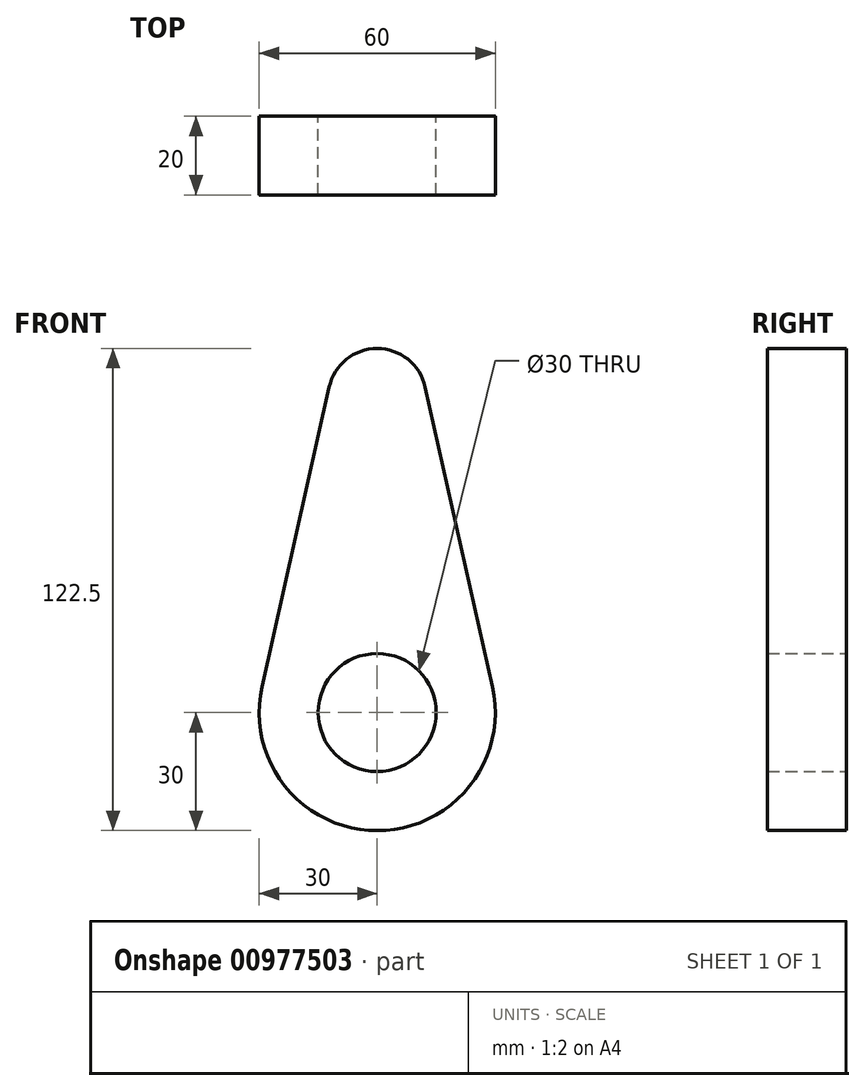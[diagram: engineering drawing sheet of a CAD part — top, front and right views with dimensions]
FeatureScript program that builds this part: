
annotation { "Feature Type Name" : "Feature", "Feature Type Description" : "" }
export const myFeature = defineFeature(function(context is Context, id is Id, definition is map)
    precondition{}
    {
        {
            var Q0;
            Q0=qCreatedBy(makeId("Front.planeOp"),FACE);
            var sketch = newSketch(context, id + "F0", { "sketchPlane" : qUnion([Q0])});
            skArc(sketch, "E0", {"start": v(-29.27, -33.44) * mm, "mid": v(0, -70) * mm, "end": v(29.27, -33.44) * mm});
            skArc(sketch, "E1", {"start": v(12.2, 42.73) * mm, "mid": v(0, 52.5) * mm, "end": v(-12.2, 42.73) * mm});
            skLineSegment(sketch, "E2", {"start": v(-12.2, 42.73) * mm, "end": v(-29.27, -33.44) * mm});
            skLineSegment(sketch, "E3", {"start": v(0, 77.79) * mm, "end": v(0, 52.5) * mm, "construction": true});
            skLineSegment(sketch, "E4.MirrorCS", {"start": v(12.2, 42.73) * mm, "end": v(29.27, -33.44) * mm});
            skPoint(sketch, "E5.orphan", {"position": v(-7, 65.88) * mm});
            skPoint(sketch, "E6.orphan", {"position": v(7, 65.88) * mm});
            skPoint(sketch, "E7.orphan", {"position": v(-36.18, -64.27) * mm});
            skPoint(sketch, "E8.orphan", {"position": v(36.18, -64.27) * mm});
            skLineSegment(sketch, "E9.trimOffspring", {"start": v(0, -70) * mm, "end": v(0, -100.52) * mm, "construction": true});
            skCircle(sketch, "E10", {"center": v(0, -40) * mm, "radius": 15 * mm});
            skSolve(sketch);
        }
        {
            var Q0;
            Q0=makeQuery(id+"F0.imprint","IMPRINT",FACE,{"disambiguationData":[TD([[makeQuery(id+"F0.imprint","IMPRINT",EDGE,{"derivedFrom":sQuery(id+"F0.wireOp",EDGE,"E0")}),1.0]])]});
            extrude(context, id + "F1", {"entities" : qUnion([Q0]), "endBound" : BoundingType.SYMMETRIC, "depth" : 20 * mm, "offsetDistance" : 25 * mm});
        }
    });
